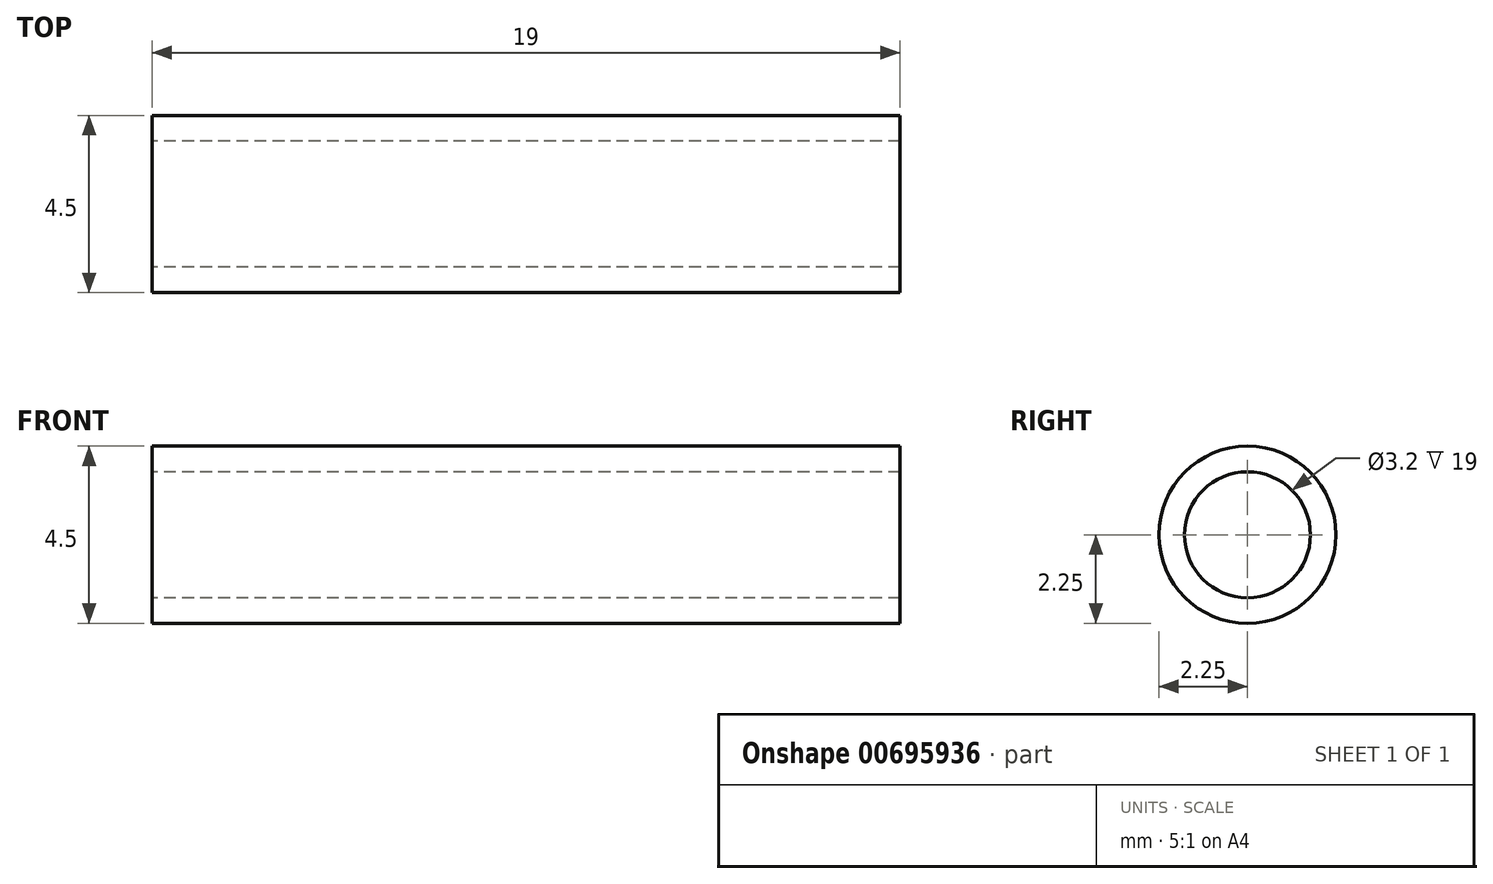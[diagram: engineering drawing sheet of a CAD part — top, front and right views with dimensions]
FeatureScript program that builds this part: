
annotation { "Feature Type Name" : "Feature", "Feature Type Description" : "" }
export const myFeature = defineFeature(function(context is Context, id is Id, definition is map)
    precondition{}
    {
        {
            var Q0;
            Q0=qCreatedBy(makeId("Right.planeOp"),FACE);
            var sketch = newSketch(context, id + "F0", { "sketchPlane" : qUnion([Q0])});
            skCircle(sketch, "E0", {"center": v(0, 0) * mm, "radius": 2.25 * mm});
            skCircle(sketch, "E1", {"center": v(0, 0) * mm, "radius": 1.6 * mm});
            skSolve(sketch);
        }
        {
            var Q0;
            Q0 = qSketchRegion(id + "F0", true);
            extrude(context, id + "F1", {"entities" : qUnion([Q0]), "endBound" : BoundingType.SYMMETRIC, "depth" : 19 * mm, "offsetDistance" : 25 * mm});
        }
    });
